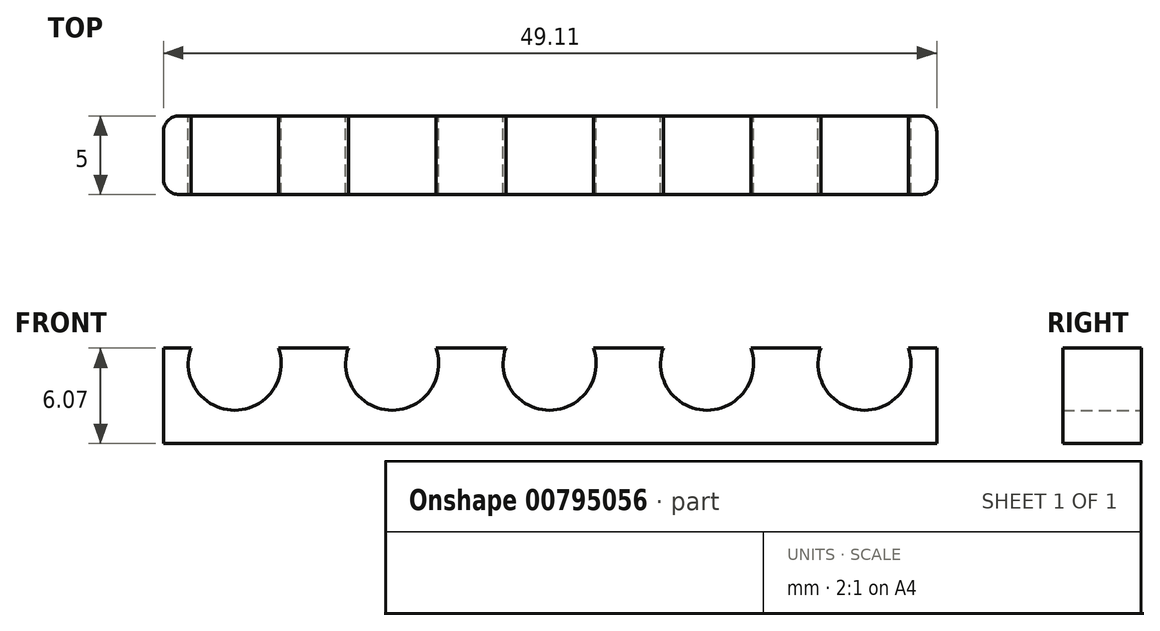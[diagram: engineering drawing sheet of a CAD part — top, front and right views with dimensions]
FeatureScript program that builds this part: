
annotation { "Feature Type Name" : "Feature", "Feature Type Description" : "" }
export const myFeature = defineFeature(function(context is Context, id is Id, definition is map)
    precondition{}
    {
        {
            var Q0;
            Q0=qCreatedBy(makeId("Front.planeOp"),FACE);
            var sketch = newSketch(context, id + "F0", { "sketchPlane" : qUnion([Q0])});
            skCircle(sketch, "E0", {"center": v(-20, 0.72) * mm, "radius": 2.95 * mm});
            skCircle(sketch, "E1.1.0.0", {"center": v(-10, 0.72) * mm, "radius": 2.95 * mm});
            skCircle(sketch, "E1.2.0.0", {"center": v(0, 0.72) * mm, "radius": 2.95 * mm});
            skCircle(sketch, "E1.3.0.0", {"center": v(10, 0.72) * mm, "radius": 2.95 * mm});
            skCircle(sketch, "E1.4.0.0", {"center": v(20, 0.72) * mm, "radius": 2.95 * mm});
            skLineSegment(sketch, "E1.direction1", {"start": v(0.3, 0.72) * mm, "end": v(10.3, 0.72) * mm, "construction": true});
            skLineSegment(sketch, "E2", {"start": v(24.59, -3.64) * mm, "end": v(-24.52, -3.64) * mm});
            skLineSegment(sketch, "E3", {"start": v(-24.52, -3.64) * mm, "end": v(-24.52, 4.45) * mm});
            skLineSegment(sketch, "E4", {"start": v(24.59, -3.64) * mm, "end": v(24.59, 4.45) * mm});
            skLineSegment(sketch, "E5", {"start": v(-24.52, 1.72) * mm, "end": v(24.59, 1.72) * mm});
            skLineSegment(sketch, "E6", {"start": v(24.59, -3.64) * mm, "end": v(24.59, -4.35) * mm});
            skLineSegment(sketch, "E7", {"start": v(24.59, -4.35) * mm, "end": v(-24.52, -4.35) * mm});
            skLineSegment(sketch, "E8", {"start": v(-24.52, -4.35) * mm, "end": v(-24.52, -3.64) * mm});
            skSolve(sketch);
        }
        {
            var Q0;
            Q0=makeQuery(id+"F0.imprint","IMPRINT",FACE,{"disambiguationData":[TD([[makeQuery(id+"F0.imprint","IMPRINT",EDGE,{"derivedFrom":sQuery(id+"F0.wireOp",EDGE,"E0")}),-1.0]])]});
            var Q1;
            Q1=makeQuery(id+"F0.imprint","IMPRINT",FACE,{"disambiguationData":[TD([[makeQuery(id+"F0.imprint","IMPRINT",EDGE,{"derivedFrom":sQuery(id+"F0.wireOp",EDGE,"E2")}),1.0]])]});
            extrude(context, id + "F1", {"entities" : qUnion([Q0, Q1]), "depth" : 5 * mm, "offsetDistance" : 25.4 * mm});
        }
        {
            var Q0;
            Q0=makeQuery(id+"F1.opExtrude","CAP_EDGE",EDGE,{"disambiguationData":[OSD([sQuery(id+"F0.wireOp",EDGE,"E4"),sQuery(id+"F0.wireOp",EDGE,"E6")])],"isStart":false});
            var Q1;
            Q1=makeQuery(id+"F1.opExtrude","CAP_EDGE",EDGE,{"disambiguationData":[OSD([sQuery(id+"F0.wireOp",EDGE,"E4"),sQuery(id+"F0.wireOp",EDGE,"E6")])],"isStart":true});
            var Q2;
            Q2=makeQuery(id+"F1.opExtrude","CAP_EDGE",EDGE,{"disambiguationData":[OSD([sQuery(id+"F0.wireOp",EDGE,"E3"),sQuery(id+"F0.wireOp",EDGE,"E8")])],"isStart":false});
            var Q3;
            Q3=makeQuery(id+"F1.opExtrude","CAP_EDGE",EDGE,{"disambiguationData":[OSD([sQuery(id+"F0.wireOp",EDGE,"E3"),sQuery(id+"F0.wireOp",EDGE,"E8")])],"isStart":true});
            fillet(context, id + "F2", {"entities" : qUnion([Q0, Q1, Q2, Q3]), "radius" : 1 * mm, "tangentPropagation" : true, "allowEdgeOverflow" : false});
        }
    });
